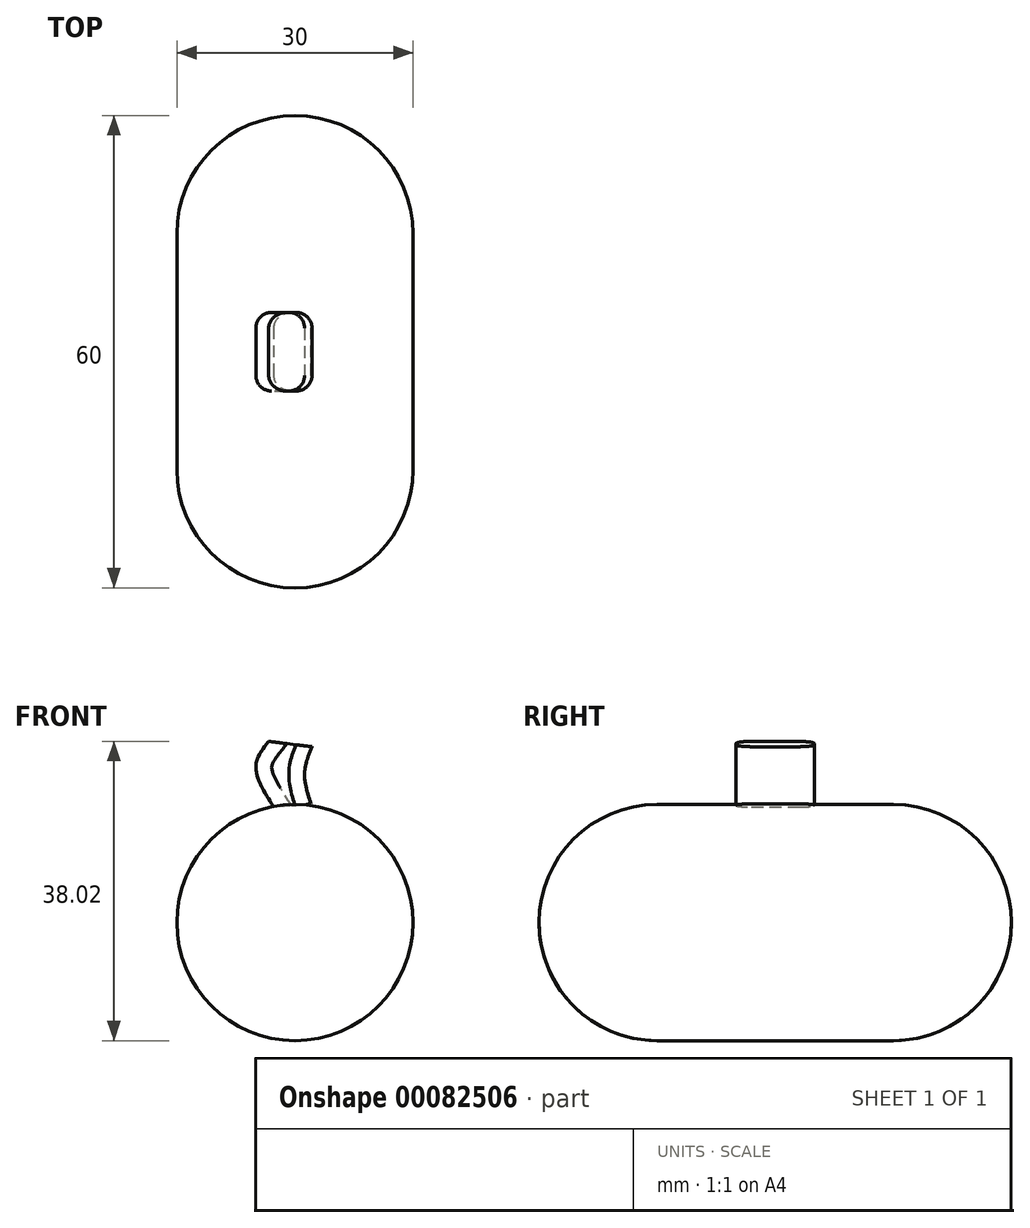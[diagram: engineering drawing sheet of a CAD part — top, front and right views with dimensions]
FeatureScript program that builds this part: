
annotation { "Feature Type Name" : "Feature", "Feature Type Description" : "" }
export const myFeature = defineFeature(function(context is Context, id is Id, definition is map)
    precondition{}
    {
        {
            var Q0;
            Q0=qCreatedBy(makeId("Front.planeOp"),FACE);
            var sketch = newSketch(context, id + "F0", { "sketchPlane" : qUnion([Q0])});
            skCircle(sketch, "E0", {"center": v(0, 0) * mm, "radius": 15 * mm});
            skSolve(sketch);
        }
        {
            var Q0;
            Q0=makeQuery(id+"F0.imprint","IMPRINT",FACE,{"disambiguationData":[TD([[makeQuery(id+"F0.imprint","IMPRINT",EDGE,{"derivedFrom":sQuery(id+"F0.wireOp",EDGE,"E0")}),1.0]])]});
            extrude(context, id + "F1", {"entities" : qUnion([Q0]), "endBound" : BoundingType.SYMMETRIC, "depth" : 60 * mm});
        }
        {
            var Q0;
            Q0=makeQuery(id+"F1.opExtrude","CAP_FACE",FACE,{"disambiguationData":[OSD([sQuery(id+"F0.wireOp",EDGE,"E0")])],"isStart":false});
            fillet(context, id + "F2", {"entities" : qUnion([Q0]), "radius" : 15 * mm, "tangentPropagation" : true, "allowEdgeOverflow" : false});
        }
        {
            var Q0;
            Q0=makeQuery(id+"F1.opExtrude","CAP_FACE",FACE,{"disambiguationData":[OSD([sQuery(id+"F0.wireOp",EDGE,"E0")])],"isStart":true});
            fillet(context, id + "F3", {"entities" : qUnion([Q0]), "radius" : 15 * mm, "tangentPropagation" : true, "allowEdgeOverflow" : false});
        }
        {
            var Q0;
            Q0=qCreatedBy(makeId("Front.planeOp"),FACE);
            var sketch = newSketch(context, id + "F4", { "sketchPlane" : qUnion([Q0])});
            skFitSpline(sketch, "E1", {"points": [v(-2.67, 14.67) * mm, v(-4.96, 19.79) * mm, v(-3.35, 23.02) * mm], "startDerivative": vector(-6.27, 9.76) * mm, "endDerivative": vector(5.35, 6.81) * mm});
            skFitSpline(sketch, "E2", {"points": [v(2.04, 15.08) * mm, v(1.23, 18.98) * mm, v(2.17, 22.34) * mm], "startDerivative": vector(-2.47, 7.71) * mm, "endDerivative": vector(2.8, 6.81) * mm});
            skLineSegment(sketch, "E3", {"start": v(-3.35, 23.02) * mm, "end": v(2.17, 22.34) * mm});
            skLineSegment(sketch, "E4", {"start": v(-2.67, 14.67) * mm, "end": v(2.04, 15.08) * mm});
            skSolve(sketch);
        }
        {
            var Q0;
            Q0=qSketchRegion(id+"F4",true);
            extrude(context, id + "F5", {"entities" : qUnion([Q0]), "endBound" : BoundingType.SYMMETRIC, "depth" : 10 * mm});
        }
        {
            var Q0;
            Q0=makeQuery(id+"F5.opExtrude","CAP_EDGE",EDGE,{"disambiguationData":[OSD([sQuery(id+"F4.wireOp",EDGE,"E2")])],"isStart":true});
            var Q1;
            Q1=makeQuery(id+"F5.opExtrude","CAP_EDGE",EDGE,{"disambiguationData":[OSD([sQuery(id+"F4.wireOp",EDGE,"E2")])],"isStart":false});
            var Q2;
            Q2=makeQuery(id+"F5.opExtrude","CAP_EDGE",EDGE,{"disambiguationData":[OSD([sQuery(id+"F4.wireOp",EDGE,"E1")])],"isStart":true});
            var Q3;
            Q3=makeQuery(id+"F5.opExtrude","CAP_EDGE",EDGE,{"disambiguationData":[OSD([sQuery(id+"F4.wireOp",EDGE,"E1")])],"isStart":false});
            fillet(context, id + "F6", {"entities" : qUnion([Q0, Q1, Q2, Q3]), "radius" : 2 * mm, "tangentPropagation" : true, "allowEdgeOverflow" : false});
        }
    });
